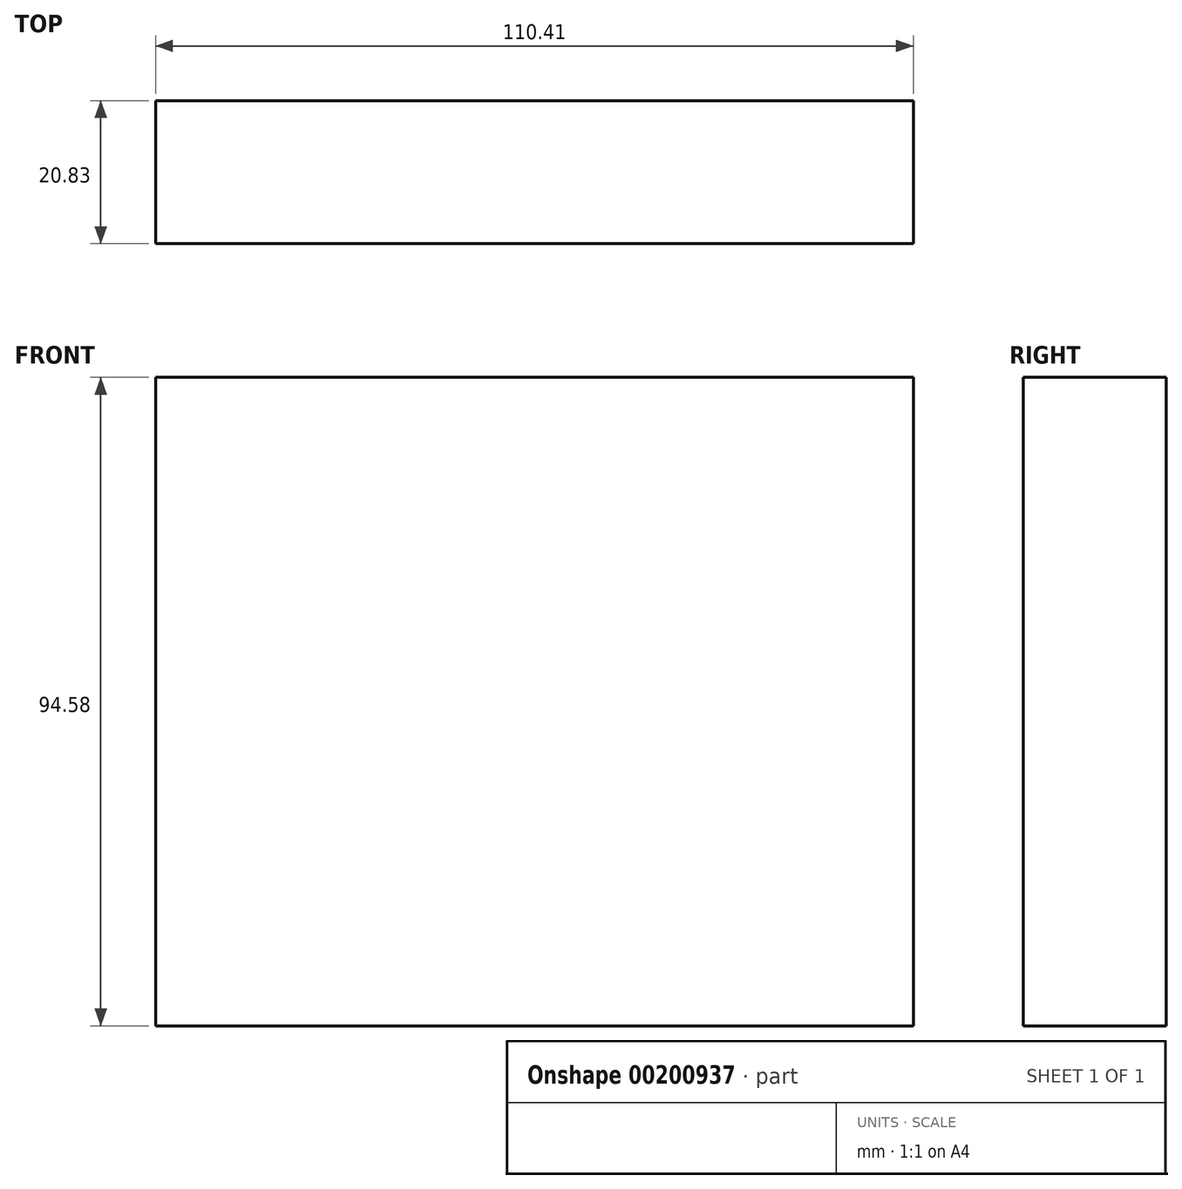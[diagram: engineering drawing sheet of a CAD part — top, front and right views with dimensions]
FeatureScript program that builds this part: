
annotation { "Feature Type Name" : "Feature", "Feature Type Description" : "" }
export const myFeature = defineFeature(function(context is Context, id is Id, definition is map)
    precondition{}
    {
        {
            var Q0;
            Q0=qCreatedBy(makeId("Front.planeOp"),FACE);
            var sketch = newSketch(context, id + "F0", { "sketchPlane" : qUnion([Q0])});
            skLineSegment(sketch, "E0.bottom", {"start": v(54.16, 47.14) * mm, "end": v(-56.25, 47.14) * mm});
            skLineSegment(sketch, "E0.top", {"start": v(54.16, -47.44) * mm, "end": v(-56.25, -47.44) * mm});
            skLineSegment(sketch, "E0.left", {"start": v(54.16, 47.14) * mm, "end": v(54.16, -47.44) * mm});
            skLineSegment(sketch, "E0.right", {"start": v(-56.25, 47.14) * mm, "end": v(-56.25, -47.44) * mm});
            skSolve(sketch);
        }
        {
            var Q0;
            Q0=makeQuery(id+"F0.imprint","IMPRINT",FACE,{"disambiguationData":[TD([[makeQuery(id+"F0.imprint","IMPRINT",EDGE,{"derivedFrom":sQuery(id+"F0.wireOp",EDGE,"E0.bottom")}),1.0]])]});
            extrude(context, id + "F1", {"entities" : qUnion([Q0]), "oppositeDirection" : true, "depth" : 20.83 * mm});
        }
    });
